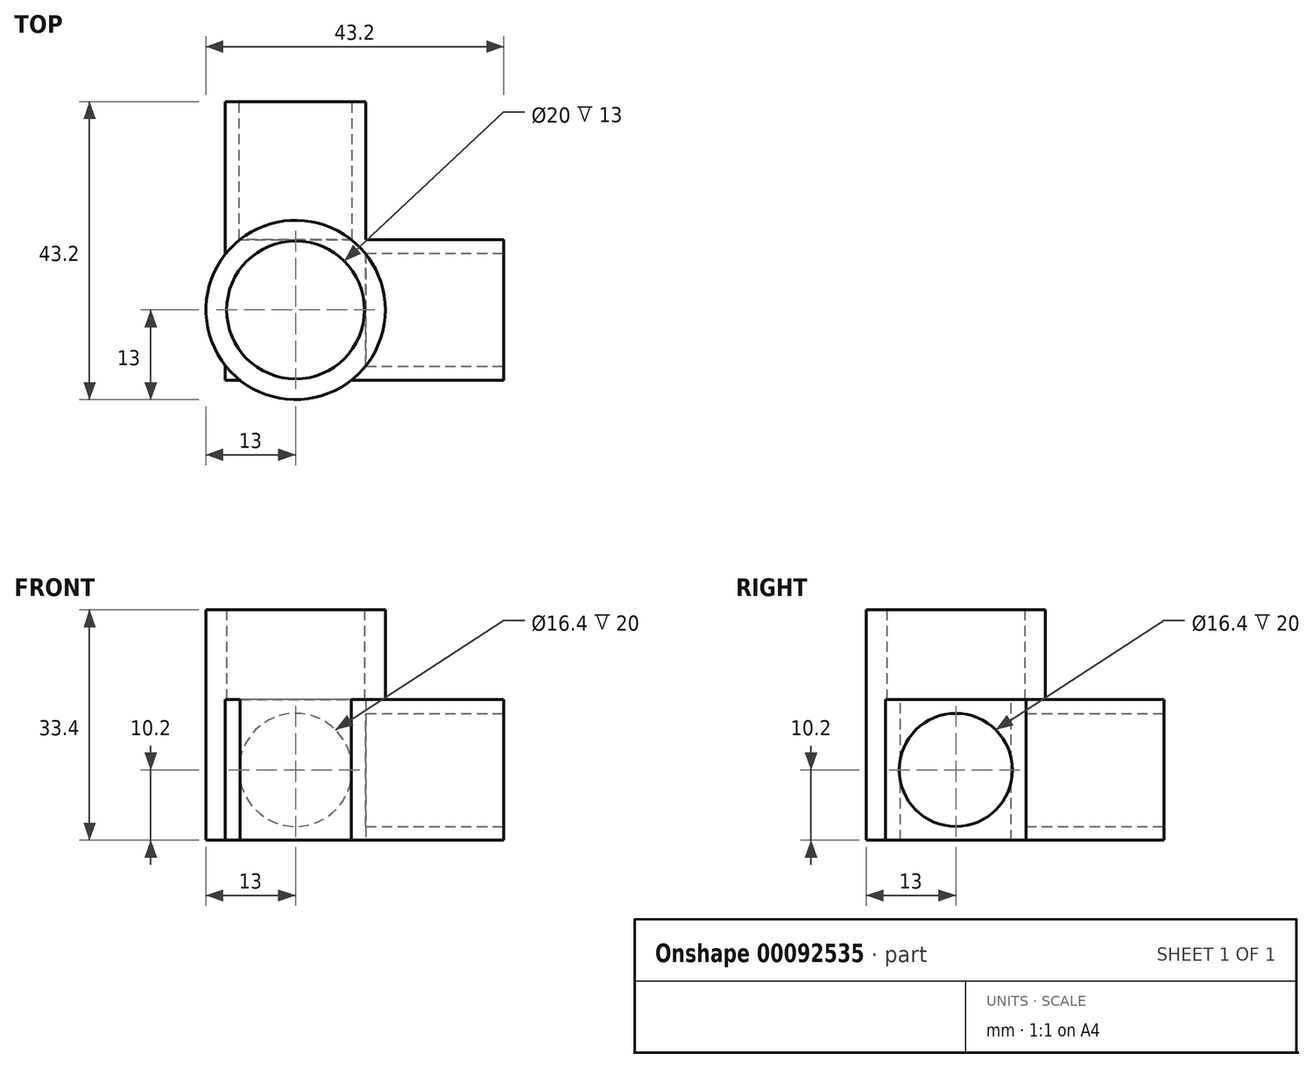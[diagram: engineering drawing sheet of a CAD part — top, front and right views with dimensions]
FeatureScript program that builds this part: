
annotation { "Feature Type Name" : "Feature", "Feature Type Description" : "" }
export const myFeature = defineFeature(function(context is Context, id is Id, definition is map)
    precondition{}
    {
        {
            var Q0;
            Q0=qCreatedBy(makeId("Top.planeOp"),FACE);
            var sketch = newSketch(context, id + "F0", { "sketchPlane" : qUnion([Q0])});
            skLineSegment(sketch, "E0", {"start": v(0, 0) * mm, "end": v(0, 40.4) * mm});
            skLineSegment(sketch, "E1", {"start": v(0, 40.4) * mm, "end": v(20.4, 40.4) * mm});
            skLineSegment(sketch, "E2", {"start": v(20.4, 40.4) * mm, "end": v(20.4, 20.4) * mm});
            skLineSegment(sketch, "E3", {"start": v(20.4, 20.4) * mm, "end": v(40.4, 20.4) * mm});
            skLineSegment(sketch, "E4", {"start": v(40.4, 20.4) * mm, "end": v(40.4, 0) * mm});
            skLineSegment(sketch, "E5", {"start": v(40.4, 0) * mm, "end": v(0, 0) * mm});
            skSolve(sketch);
        }
        {
            var Q0;
            Q0=makeQuery(id+"F0.imprint","IMPRINT",FACE,{"disambiguationData":[TD([[makeQuery(id+"F0.imprint","IMPRINT",EDGE,{"derivedFrom":sQuery(id+"F0.wireOp",EDGE,"E0")}),-1.0]])]});
            extrude(context, id + "F1", {"entities" : qUnion([Q0]), "depth" : 20.4 * mm});
        }
        {
            var Q0;
            Q0=makeQuery(id+"F1.opExtrude","SWEPT_FACE",FACE,{"disambiguationData":[OSD([sQuery(id+"F0.wireOp",EDGE,"E4")])]});
            var sketch = newSketch(context, id + "F2", { "sketchPlane" : qUnion([Q0])});
            skCircle(sketch, "E6", {"center": v(10.2, 10.2) * mm, "radius": 8.2 * mm});
            skLineSegment(sketch, "E7", {"start": v(10.2, 10.2) * mm, "end": v(10.2, 0) * mm});
            skLineSegment(sketch, "E8", {"start": v(10.2, 10.2) * mm, "end": v(20.4, 10.2) * mm});
            skSolve(sketch);
        }
        {
            var Q0;
            Q0=makeQuery(id+"F1.opExtrude","SWEPT_FACE",FACE,{"disambiguationData":[OSD([sQuery(id+"F0.wireOp",EDGE,"E1")])]});
            var sketch = newSketch(context, id + "F3", { "sketchPlane" : qUnion([Q0])});
            skCircle(sketch, "E9", {"center": v(-10.2, 10.2) * mm, "radius": 8.2 * mm});
            skLineSegment(sketch, "E10", {"start": v(-10.2, 10.2) * mm, "end": v(0, 10.2) * mm});
            skLineSegment(sketch, "E11", {"start": v(0, 10.2) * mm, "end": v(-10.2, 10.2) * mm});
            skLineSegment(sketch, "E12", {"start": v(-10.2, 10.2) * mm, "end": v(-10.2, 0) * mm});
            skSolve(sketch);
        }
        {
            var Q0;
            {var subQ0=sQuery(id+"F3.wireOp",EDGE,"E11");var subQ1=sQuery(id+"F3.wireOp",EDGE,"E9");var subQ2=makeQuery(id+"F3.imprint","INTERSECT",VERTEX,{"derivedFrom":[subQ1,subQ0]});Q0=makeQuery(id+"F3.imprint","IMPRINT",FACE,{"disambiguationData":[TD([[makeQuery(id+"F3.imprint","IMPRINT",EDGE,{"disambiguationData":[TD([[subQ2,-1.0]])],"derivedFrom":subQ1}),1.0]])]});}
            var Q1;
            {var subQ0=sQuery(id+"F3.wireOp",EDGE,"E11");var subQ1=sQuery(id+"F3.wireOp",EDGE,"E9");var subQ2=makeQuery(id+"F3.imprint","INTERSECT",VERTEX,{"derivedFrom":[subQ1,subQ0]});Q1=makeQuery(id+"F3.imprint","IMPRINT",FACE,{"disambiguationData":[TD([[makeQuery(id+"F3.imprint","IMPRINT",EDGE,{"disambiguationData":[TD([[subQ2,1.0]])],"derivedFrom":subQ1}),1.0]])]});}
            var Q2;
            Q2=sQuery(id+"F3.wireOp",EDGE,"E9");
            extrude(context, id + "F4", {"entities" : qUnion([Q0, Q1]), "operationType" : NewBodyOperationType.REMOVE, "surfaceEntities" : qUnion([Q2]), "oppositeDirection" : true, "depth" : 20 * mm});
        }
        {
            var Q0;
            {var subQ0=sQuery(id+"F2.wireOp",EDGE,"E7");var subQ1=sQuery(id+"F2.wireOp",EDGE,"E6");var subQ2=makeQuery(id+"F2.imprint","INTERSECT",VERTEX,{"derivedFrom":[subQ1,subQ0]});Q0=makeQuery(id+"F2.imprint","IMPRINT",FACE,{"disambiguationData":[TD([[makeQuery(id+"F2.imprint","IMPRINT",EDGE,{"disambiguationData":[TD([[subQ2,-1.0]])],"derivedFrom":subQ1}),1.0]])]});}
            var Q1;
            {var subQ0=sQuery(id+"F2.wireOp",EDGE,"E7");var subQ1=sQuery(id+"F2.wireOp",EDGE,"E6");var subQ2=makeQuery(id+"F2.imprint","INTERSECT",VERTEX,{"derivedFrom":[subQ1,subQ0]});Q1=makeQuery(id+"F2.imprint","IMPRINT",FACE,{"disambiguationData":[TD([[makeQuery(id+"F2.imprint","IMPRINT",EDGE,{"disambiguationData":[TD([[subQ2,1.0]])],"derivedFrom":subQ1}),1.0]])]});}
            var Q2;
            Q2=sQuery(id+"F2.wireOp",EDGE,"E6");
            extrude(context, id + "F5", {"entities" : qUnion([Q0, Q1]), "operationType" : NewBodyOperationType.REMOVE, "surfaceEntities" : qUnion([Q2]), "oppositeDirection" : true, "depth" : 20 * mm});
        }
        {
            var Q0;
            Q0=makeQuery(id+"F1.opExtrude","CAP_FACE",FACE,{"disambiguationData":[OSD([sQuery(id+"F0.wireOp",EDGE,"E0"),sQuery(id+"F0.wireOp",EDGE,"E1"),sQuery(id+"F0.wireOp",EDGE,"E2"),sQuery(id+"F0.wireOp",EDGE,"E3"),sQuery(id+"F0.wireOp",EDGE,"E4"),sQuery(id+"F0.wireOp",EDGE,"E5")])],"isStart":false});
            var sketch = newSketch(context, id + "F6", { "sketchPlane" : qUnion([Q0])});
            skLineSegment(sketch, "E13", {"start": v(0, 0) * mm, "end": v(20.4, 20.4) * mm});
            skCircle(sketch, "E14", {"center": v(10.2, 10.2) * mm, "radius": 13 * mm});
            skCircle(sketch, "E15", {"center": v(10.2, 10.2) * mm, "radius": 10 * mm});
            skLineSegment(sketch, "E16", {"start": v(2.14, 0) * mm, "end": v(18.26, 0) * mm});
            skLineSegment(sketch, "E17", {"start": v(0, 2.14) * mm, "end": v(0, 18.26) * mm});
            skSolve(sketch);
        }
        {
            var Q0;
            {var subQ0=sQuery(id+"F6.wireOp",EDGE,"E16");Q0=makeQuery(id+"F6.imprint","IMPRINT",FACE,{"disambiguationData":[TD([[makeQuery(id+"F6.imprint","IMPRINT",EDGE,{"derivedFrom":subQ0}),1.0]])]});}
            var Q1;
            {var subQ0=sQuery(id+"F6.wireOp",EDGE,"E17");Q1=makeQuery(id+"F6.imprint","IMPRINT",FACE,{"disambiguationData":[TD([[makeQuery(id+"F6.imprint","IMPRINT",EDGE,{"derivedFrom":subQ0}),1.0]])]});}
            var Q2;
            {var subQ0=sQuery(id+"F6.wireOp",EDGE,"E16");Q2=makeQuery(id+"F6.imprint","IMPRINT",FACE,{"disambiguationData":[TD([[makeQuery(id+"F6.imprint","IMPRINT",EDGE,{"derivedFrom":subQ0}),-1.0]])]});}
            var Q3;
            {var subQ0=sQuery(id+"F6.wireOp",EDGE,"E17");Q3=makeQuery(id+"F6.imprint","IMPRINT",FACE,{"disambiguationData":[TD([[makeQuery(id+"F6.imprint","IMPRINT",EDGE,{"derivedFrom":subQ0}),-1.0]])]});}
            extrude(context, id + "F7", {"entities" : qUnion([Q0, Q1, Q2, Q3]), "operationType" : NewBodyOperationType.ADD, "depth" : 13 * mm});
        }
        {
            var Q0;
            {var subQ0=sQuery(id+"F6.wireOp",EDGE,"E16");Q0=makeQuery(id+"F6.imprint","IMPRINT",FACE,{"disambiguationData":[TD([[makeQuery(id+"F6.imprint","IMPRINT",EDGE,{"derivedFrom":subQ0}),1.0]])]});}
            extrude(context, id + "F8", {"entities" : qUnion([Q0]), "operationType" : NewBodyOperationType.ADD, "oppositeDirection" : true, "depth" : 20.4 * mm});
        }
        {
            var Q0;
            {var subQ0=sQuery(id+"F6.wireOp",EDGE,"E17");Q0=makeQuery(id+"F6.imprint","IMPRINT",FACE,{"disambiguationData":[TD([[makeQuery(id+"F6.imprint","IMPRINT",EDGE,{"derivedFrom":subQ0}),1.0]])]});}
            extrude(context, id + "F9", {"entities" : qUnion([Q0]), "operationType" : NewBodyOperationType.ADD, "oppositeDirection" : true, "depth" : 20.4 * mm});
        }
    });
